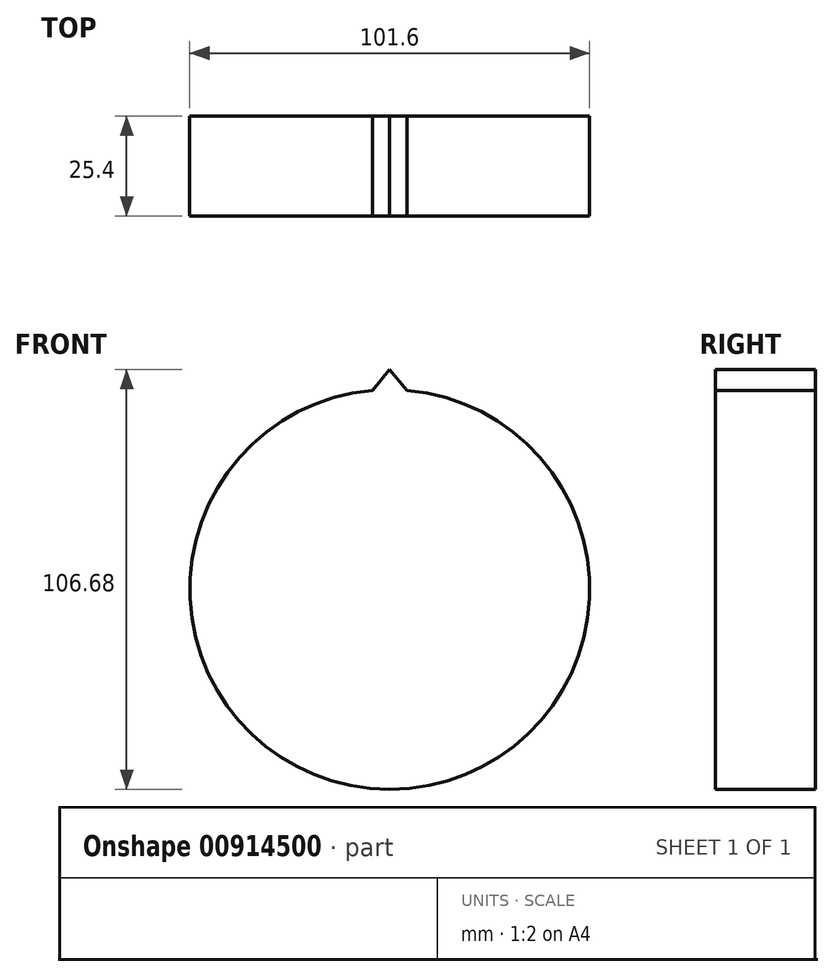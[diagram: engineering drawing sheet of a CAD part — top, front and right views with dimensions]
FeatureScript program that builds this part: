
annotation { "Feature Type Name" : "Feature", "Feature Type Description" : "" }
export const myFeature = defineFeature(function(context is Context, id is Id, definition is map)
    precondition{}
    {
        {
            var Q0;
            Q0=qCreatedBy(makeId("Front.planeOp"),FACE);
            var sketch = newSketch(context, id + "F0", { "sketchPlane" : qUnion([Q0])});
            skCircle(sketch, "E0", {"center": v(0, 0) * mm, "radius": 50.8 * mm});
            skSolve(sketch);
        }
        {
            var Q0;
            Q0 = qSketchRegion(id + "F0", true);
            extrude(context, id + "F1", {"entities" : qUnion([Q0]), "depth" : 25.4 * mm, "offsetDistance" : 25.4 * mm});
        }
        {
            var Q0;
            Q0=qCreatedBy(makeId("Front.planeOp"),FACE);
            var sketch = newSketch(context, id + "F2", { "sketchPlane" : qUnion([Q0])});
            skLineSegment(sketch, "E1", {"start": v(0, 55.88) * mm, "end": v(-4.43, 50.6) * mm});
            skLineSegment(sketch, "E2", {"start": v(-4.43, 50.6) * mm, "end": v(4.43, 50.6) * mm});
            skLineSegment(sketch, "E3", {"start": v(4.43, 50.6) * mm, "end": v(0, 55.88) * mm});
            skPoint(sketch, "E4", {"position": v(0, 50.6) * mm});
            skLineSegment(sketch, "E5", {"start": v(4.43, 50.6) * mm, "end": v(0, 0) * mm, "construction": true});
            skLineSegment(sketch, "E6", {"start": v(0, 0) * mm, "end": v(-4.43, 50.6) * mm, "construction": true});
            skSolve(sketch);
        }
        {
            var Q0;
            Q0=makeQuery(id+"F2.imprint","IMPRINT",FACE,{"disambiguationData":[TD([[makeQuery(id+"F2.imprint","IMPRINT",EDGE,{"derivedFrom":sQuery(id+"F2.wireOp",EDGE,"E1")}),1.0]])]});
            var Q1;
            Q1=makeQuery(id+"F1.opExtrude","CAP_FACE",FACE,{"disambiguationData":[OSD([sQuery(id+"F0.wireOp",EDGE,"E0")])],"isStart":false});
            extrude(context, id + "F3", {"entities" : qUnion([Q0]), "operationType" : NewBodyOperationType.ADD, "endBound" : BoundingType.UP_TO_SURFACE, "depth" : 25.4 * mm, "endBoundEntityFace" : qUnion([Q1]), "offsetDistance" : 25.4 * mm});
        }
        {
            var Q0;
            Q0=qCreatedBy(makeId("Top.planeOp"),FACE);
            var sketch = newSketch(context, id + "F4", { "sketchPlane" : qUnion([Q0])});
            skLineSegment(sketch, "E7", {"start": v(0, 0) * mm, "end": v(0, -55.49) * mm, "construction": true});
            skSolve(sketch);
        }
    });
